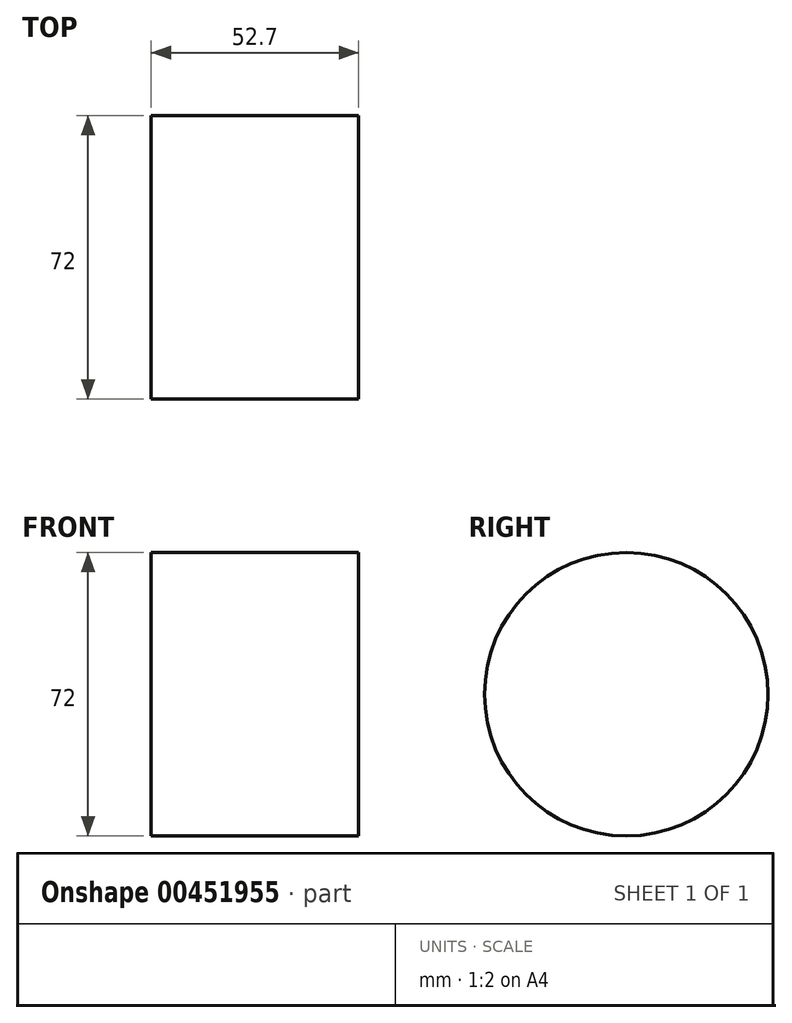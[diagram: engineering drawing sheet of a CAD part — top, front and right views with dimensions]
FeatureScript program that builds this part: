
annotation { "Feature Type Name" : "Feature", "Feature Type Description" : "" }
export const myFeature = defineFeature(function(context is Context, id is Id, definition is map)
    precondition{}
    {
        {
            var Q0;
            Q0=qCreatedBy(makeId("Right.planeOp"),FACE);
            var sketch = newSketch(context, id + "F0", { "sketchPlane" : qUnion([Q0])});
            skCircle(sketch, "E0", {"center": v(0, 0) * mm, "radius": 36 * mm});
            skSolve(sketch);
        }
        {
            var Q0;
            Q0=makeQuery(id+"F0.imprint","IMPRINT",FACE,{"disambiguationData":[TD([[makeQuery(id+"F0.imprint","IMPRINT",EDGE,{"derivedFrom":sQuery(id+"F0.wireOp",EDGE,"E0")}),1.0]])]});
            extrude(context, id + "F1", {"entities" : qUnion([Q0]), "depth" : 52.7 * mm});
        }
    });
